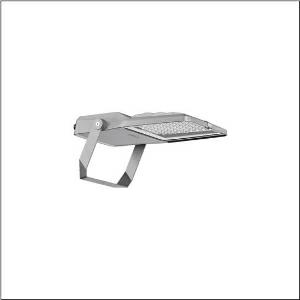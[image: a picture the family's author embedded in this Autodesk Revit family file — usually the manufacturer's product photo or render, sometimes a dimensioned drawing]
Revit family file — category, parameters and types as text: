
# Revit family: floodlight_fl_21_iq_mini___pl33t_5xa7771b2f1a_e875
name_source: partatom
category: Lighting Fixtures
units: mm (PartAtom-declared; Revit-internal decimal feet)

## family parameters
Cut with Voids When Loaded = No
Host = Face
Light Source = No
Part Type = Normal
Room Calculation Point = No
Round Connector Dimension = Use Diameter
Shared = No

## types (1)
- --- (1 x LED, 6170 lm, 45.5 W, 3000K)
    Apparent Load = 46 VA
    CIE Flux Codes = 26 75 99 100 100
    Color Rendering = 70
    Color Temperature = 3000K
    Default Elevation = 1800 mm
    Description = Floodlight FL 21 iQ mini, floodlight, primary light control with lens, of PMMA, primary optical cover: protective disc, of toughened safety glass, transparent, light distribution: PL33T, light emission: direct distribution, installation type: surface-mounted, LED, High Power LED, rated luminous flux: 6.170lm, luminous efficacy: 136lm/W, light colour: 730, colour temperature: 3000K, control gear: iQ Comfort/DALI, control: Auto-Match, Temp-Guard, Lumen-Switch, Night-Set, Smart-Wire, Light-Fading, Desk-Remote (wireless, voltage-free reading and setting of iQ features in the workshop via application-optimized NFC function/RFID function), optimised constant luminous flux control (CLO 2.0), with terminal, 6-pole, mains connection: 220..240V, AC, 50/60Hz, start of lifetime: 46W, end of service life: 48W, reduction: 22W, luminaire housing, of diecast aluminium, powder-coated, Siteco® metallic grey (DB 702S), corrosivity category C5 mid according to DIN EN ISO 12944, suitable for swimming pools, chlorine-resistant, sealing non-destructively replaceable, mounting bracket, of steel, galvanised, powder-coated, Siteco® metallic grey (DB 702S), protection rating (complete): IP66, insulation class (complete): insulation class II (safety insulation), certification: CE, ENEC, VDE, protection symbol: D, impact resistance: IK08, permissible operating ambient temperature: -40..+40°C, permissible operating ambient temperature for outdoor applications: -40..+50°C, standard: DIN EN 12944, LABS conformity tested according to VDMA 24364:2018-05, packaging unit: 1 piece

Light Distribution: PL33T
    Height = 70 mm
    Lamp = 1 x LED
    Lamp Light Flux = 6170 lm
    Lamp Power = 45.5 W
    Lamp count = 1
    Length = 485 mm
    Luminous efficacy = 136 lm/W
    Manufacturer = Siteco
    ModVariant = No
    Model = 5XA7771B2F1A
    Mounting Place = Wall
    Mounting Type = Surface mounted
    Number of Poles = 1
    OnlyDefault = Yes
    Power Factor = 1
    Product Name = Floodlight FL 21 iQ mini | PL33T
    Product group = floodlight | wall mounted
    ProductGroupID = 2001
    Protection Class = Protection class II
    Protection Degree = IP 66
    RLX_Detail_Level = 1
    RLX_Emergency_Light_Flux = 0 lm
    RLX_Emergency_Type = 0
    RLX_Emergency_Type_DB = No
    RlxData = <blob elided: 96165 chars, md5=5e35cebc>
    Socket = socket
    Standby Power = 0 W
    System Light Flux = 6170 lm
    System Power = 46 W
    Type Comments = factory setting: luminous flux: 100 % | dim-lin: 254 | 463 mA
    Type Image = l_1006845.jpg
    URL = http://relux.com
    VarID = @adj_150356
    Voltage = 0 V
    Weight = 0.00 kg
    Width = 337 mm

## geometry (parser evidence)
native form markers: Blend x4, Sweep x13
no freeform markers — native parametric forms only
